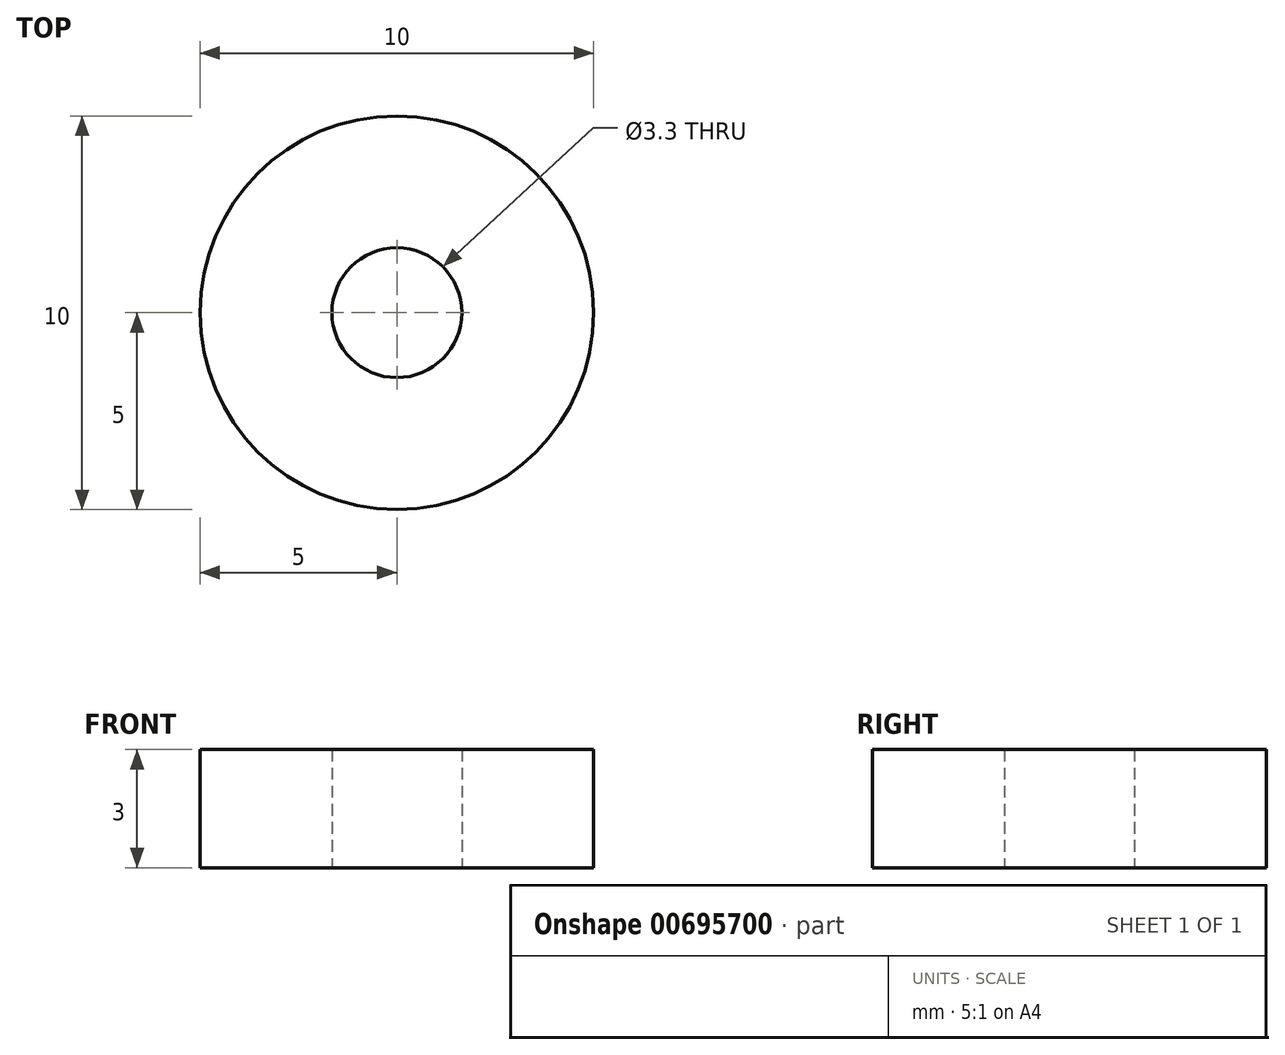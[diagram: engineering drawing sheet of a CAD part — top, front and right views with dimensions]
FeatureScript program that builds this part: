
annotation { "Feature Type Name" : "Feature", "Feature Type Description" : "" }
export const myFeature = defineFeature(function(context is Context, id is Id, definition is map)
    precondition{}
    {
        {
            var Q0;
            Q0=qCreatedBy(makeId("Top.planeOp"),FACE);
            var sketch = newSketch(context, id + "F0", { "sketchPlane" : qUnion([Q0])});
            skCircle(sketch, "E0", {"center": v(0, 0) * mm, "radius": 5 * mm});
            skCircle(sketch, "E1", {"center": v(0, 0) * mm, "radius": 1.65 * mm});
            skSolve(sketch);
        }
        {
            var Q0;
            Q0=makeQuery(id+"F0.imprint","IMPRINT",FACE,{"disambiguationData":[TD([[makeQuery(id+"F0.imprint","IMPRINT",EDGE,{"derivedFrom":sQuery(id+"F0.wireOp",EDGE,"E0")}),1.0]])]});
            extrude(context, id + "F1", {"entities" : qUnion([Q0]), "depth" : 3 * mm, "offsetDistance" : 25 * mm});
        }
    });
